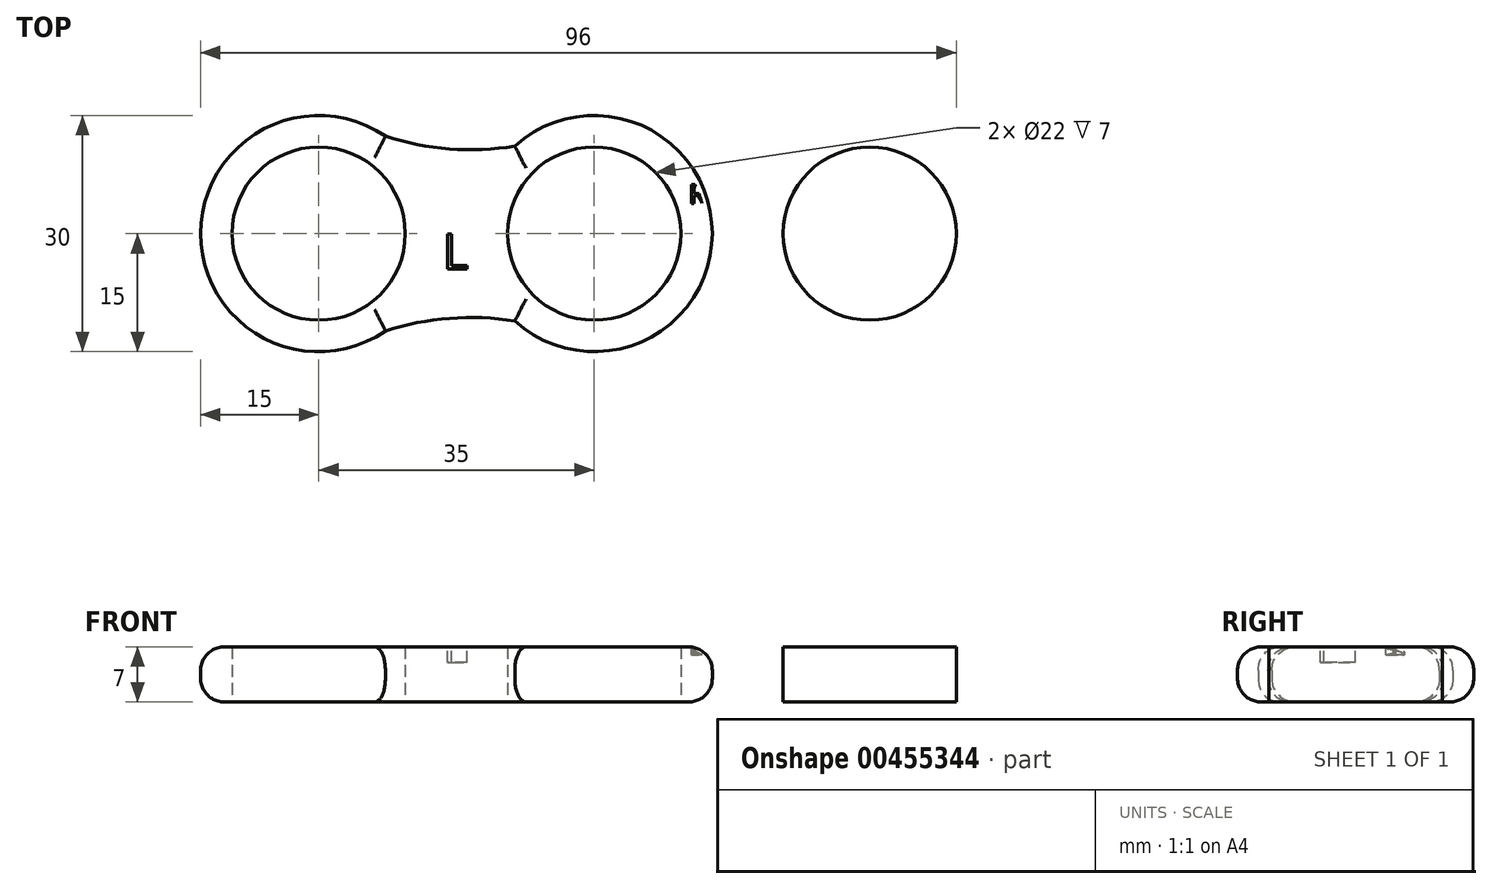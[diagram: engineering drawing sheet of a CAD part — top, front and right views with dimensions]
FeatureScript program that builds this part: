
annotation { "Feature Type Name" : "Feature", "Feature Type Description" : "" }
export const myFeature = defineFeature(function(context is Context, id is Id, definition is map)
    precondition{}
    {
        {
            var Q0;
            Q0=qCreatedBy(makeId("Top.planeOp"),FACE);
            var sketch = newSketch(context, id + "F0", { "sketchPlane" : qUnion([Q0])});
            skPoint(sketch, "E0.middle", {"position": v(0, 0) * mm});
            skCircle(sketch, "E1", {"center": v(0, 0) * mm, "radius": 11 * mm});
            skCircle(sketch, "E2", {"center": v(0, 0) * mm, "radius": 15 * mm});
            skCircle(sketch, "E3", {"center": v(-35, 0) * mm, "radius": 11 * mm});
            skCircle(sketch, "E4", {"center": v(-35, 0) * mm, "radius": 15 * mm});
            skArc(sketch, "E5", {"start": v(-26.52, 12.37) * mm, "mid": v(-18.37, 10.76) * mm, "end": v(-10.08, 11.11) * mm});
            skArc(sketch, "E6.MirrorCS", {"start": v(-26.52, -12.37) * mm, "mid": v(-18.37, -10.76) * mm, "end": v(-10.08, -11.11) * mm});
            skArc(sketch, "E7.MirrorCS", {"start": v(26.52, 12.37) * mm, "mid": v(18.37, 10.76) * mm, "end": v(10.08, 11.11) * mm});
            skArc(sketch, "E8.MirrorCS", {"start": v(26.52, -12.37) * mm, "mid": v(18.37, -10.76) * mm, "end": v(10.08, -11.11) * mm});
            skCircle(sketch, "E9.MirrorC", {"center": v(35, 0) * mm, "radius": 15 * mm});
            skCircle(sketch, "E10.MirrorC", {"center": v(35, 0) * mm, "radius": 11 * mm});
            skSolve(sketch);
        }
        {
            var Q0;
            Q0=makeQuery(id+"F0.imprint","IMPRINT",FACE,{"disambiguationData":[TD([[makeQuery(id+"F0.imprint","IMPRINT",EDGE,{"derivedFrom":sQuery(id+"F0.wireOp",EDGE,"cd22e090-de5e-44ce-a2e8-da55deea97581.MirrorC")}),1.0]])]});
            var Q1;
            Q1=makeQuery(id+"F0.imprint","IMPRINT",FACE,{"disambiguationData":[TD([[makeQuery(id+"F0.imprint","IMPRINT",EDGE,{"derivedFrom":sQuery(id+"F0.wireOp",EDGE,"E1")}),-1.0]])]});
            var Q2;
            {var subQ0=sQuery(id+"F0.wireOp",EDGE,"e8e17bcd-66d5-45fb-b403-fcb8348c6d070.MirrorCS");Q2=makeQuery(id+"F0.imprint","IMPRINT",FACE,{"disambiguationData":[TD([[makeQuery(id+"F0.imprint","IMPRINT",EDGE,{"derivedFrom":subQ0}),-1.0]])]});}
            var Q3;
            {var subQ0=sQuery(id+"F0.wireOp",EDGE,"E5");Q3=makeQuery(id+"F0.imprint","IMPRINT",FACE,{"disambiguationData":[TD([[makeQuery(id+"F0.imprint","IMPRINT",EDGE,{"derivedFrom":subQ0}),-1.0]])]});}
            var Q4;
            Q4=makeQuery(id+"F0.imprint","IMPRINT",FACE,{"disambiguationData":[TD([[makeQuery(id+"F0.imprint","IMPRINT",EDGE,{"derivedFrom":sQuery(id+"F0.wireOp",EDGE,"E3")}),-1.0]])]});
            var Q5;
            Q5=makeQuery(id+"F0.imprint","IMPRINT",FACE,{"disambiguationData":[TD([[makeQuery(id+"F0.imprint","IMPRINT",EDGE,{"derivedFrom":sQuery(id+"F0.wireOp",EDGE,"E10.MirrorC")}),1.0]])]});
            var Q6;
            {var subQ0=sQuery(id+"F0.wireOp",EDGE,"E7.MirrorCS");Q6=makeQuery(id+"F0.imprint","IMPRINT",FACE,{"disambiguationData":[TD([[makeQuery(id+"F0.imprint","IMPRINT",EDGE,{"derivedFrom":subQ0}),1.0]])]});}
            extrude(context, id + "F1", {"entities" : qUnion([Q0, Q1, Q2, Q3, Q4, Q5, Q6]), "depth" : 7 * mm});
        }
        {
            var Q0;
            Q0=makeQuery(id+"F1.opExtrude","CAP_EDGE",EDGE,{"disambiguationData":[OSD([sQuery(id+"F0.wireOp",EDGE,"E5")])],"isStart":true});
            var Q1;
            Q1=makeQuery(id+"F1.opExtrude","CAP_EDGE",EDGE,{"disambiguationData":[OSD([sQuery(id+"F0.wireOp",EDGE,"E4")])],"isStart":true});
            var Q2;
            Q2=makeQuery(id+"F1.opExtrude","CAP_EDGE",EDGE,{"disambiguationData":[OSD([sQuery(id+"F0.wireOp",EDGE,"E6.MirrorCS")])],"isStart":true});
            var Q3;
            {var subQ0=sQuery(id+"F0.wireOp",EDGE,"E2");Q3=makeQuery(id+"F1.opExtrude","CAP_EDGE",EDGE,{"disambiguationData":[OSD([subQ0]),TDD([makeQuery(id+"F0.imprint","IMPRINT",EDGE,{"disambiguationData":[TD([[makeQuery(id+"F0.imprint","INTERSECT",VERTEX,{"derivedFrom":[subQ0,sQuery(id+"F0.wireOp",EDGE,"E6.MirrorCS")]}),-1.0]])],"derivedFrom":subQ0})])],"isStart":true});}
            var Q4;
            Q4=makeQuery(id+"F1.opExtrude","CAP_EDGE",EDGE,{"disambiguationData":[OSD([sQuery(id+"F0.wireOp",EDGE,"E8.MirrorCS")])],"isStart":true});
            var Q5;
            Q5=makeQuery(id+"F1.opExtrude","CAP_EDGE",EDGE,{"disambiguationData":[OSD([sQuery(id+"F0.wireOp",EDGE,"E9.MirrorC")])],"isStart":true});
            var Q6;
            Q6=makeQuery(id+"F1.opExtrude","CAP_EDGE",EDGE,{"disambiguationData":[OSD([sQuery(id+"F0.wireOp",EDGE,"E7.MirrorCS")])],"isStart":true});
            var Q7;
            {var subQ0=sQuery(id+"F0.wireOp",EDGE,"E2");Q7=makeQuery(id+"F1.opExtrude","CAP_EDGE",EDGE,{"disambiguationData":[OSD([subQ0]),TDD([makeQuery(id+"F0.imprint","IMPRINT",EDGE,{"disambiguationData":[TD([[makeQuery(id+"F0.imprint","INTERSECT",VERTEX,{"derivedFrom":[subQ0,sQuery(id+"F0.wireOp",EDGE,"E5")]}),1.0]])],"derivedFrom":subQ0})])],"isStart":true});}
            fillet(context, id + "F2", {"entities" : qUnion([Q0, Q1, Q2, Q3, Q4, Q5, Q6, Q7]), "radius" : 3 * mm, "tangentPropagation" : true, "allowEdgeOverflow" : false});
        }
        {
            var Q0;
            Q0=makeQuery(id+"F1.opExtrude","CAP_EDGE",EDGE,{"disambiguationData":[OSD([sQuery(id+"F0.wireOp",EDGE,"E9.MirrorC")])],"isStart":false});
            var Q1;
            Q1=makeQuery(id+"F1.opExtrude","CAP_EDGE",EDGE,{"disambiguationData":[OSD([sQuery(id+"F0.wireOp",EDGE,"E8.MirrorCS")])],"isStart":false});
            var Q2;
            {var subQ0=sQuery(id+"F0.wireOp",EDGE,"E2");Q2=makeQuery(id+"F1.opExtrude","CAP_EDGE",EDGE,{"disambiguationData":[OSD([subQ0]),TDD([makeQuery(id+"F0.imprint","IMPRINT",EDGE,{"disambiguationData":[TD([[makeQuery(id+"F0.imprint","INTERSECT",VERTEX,{"derivedFrom":[subQ0,sQuery(id+"F0.wireOp",EDGE,"E6.MirrorCS")]}),-1.0]])],"derivedFrom":subQ0})])],"isStart":false});}
            var Q3;
            Q3=makeQuery(id+"F1.opExtrude","CAP_EDGE",EDGE,{"disambiguationData":[OSD([sQuery(id+"F0.wireOp",EDGE,"E6.MirrorCS")])],"isStart":false});
            var Q4;
            Q4=makeQuery(id+"F1.opExtrude","CAP_EDGE",EDGE,{"disambiguationData":[OSD([sQuery(id+"F0.wireOp",EDGE,"E4")])],"isStart":false});
            var Q5;
            Q5=makeQuery(id+"F1.opExtrude","CAP_EDGE",EDGE,{"disambiguationData":[OSD([sQuery(id+"F0.wireOp",EDGE,"E5")])],"isStart":false});
            var Q6;
            {var subQ0=sQuery(id+"F0.wireOp",EDGE,"E2");Q6=makeQuery(id+"F1.opExtrude","CAP_EDGE",EDGE,{"disambiguationData":[OSD([subQ0]),TDD([makeQuery(id+"F0.imprint","IMPRINT",EDGE,{"disambiguationData":[TD([[makeQuery(id+"F0.imprint","INTERSECT",VERTEX,{"derivedFrom":[subQ0,sQuery(id+"F0.wireOp",EDGE,"E5")]}),1.0]])],"derivedFrom":subQ0})])],"isStart":false});}
            var Q7;
            Q7=makeQuery(id+"F1.opExtrude","CAP_EDGE",EDGE,{"disambiguationData":[OSD([sQuery(id+"F0.wireOp",EDGE,"E7.MirrorCS")])],"isStart":false});
            fillet(context, id + "F3", {"entities" : qUnion([Q0, Q1, Q2, Q3, Q4, Q5, Q6, Q7]), "radius" : 3 * mm, "tangentPropagation" : true, "allowEdgeOverflow" : false});
        }
        {
            var Q0;
            Q0=makeQuery(id+"F1.opExtrude","CAP_FACE",FACE,{"disambiguationData":[OSD([sQuery(id+"F0.wireOp",EDGE,"E1"),sQuery(id+"F0.wireOp",EDGE,"E2"),sQuery(id+"F0.wireOp",EDGE,"E3"),sQuery(id+"F0.wireOp",EDGE,"E4"),sQuery(id+"F0.wireOp",EDGE,"E5"),sQuery(id+"F0.wireOp",EDGE,"E6.MirrorCS"),sQuery(id+"F0.wireOp",EDGE,"E7.MirrorCS"),sQuery(id+"F0.wireOp",EDGE,"E8.MirrorCS"),sQuery(id+"F0.wireOp",EDGE,"E9.MirrorC"),sQuery(id+"F0.wireOp",EDGE,"E10.MirrorC")])],"isStart":false});
            var sketch = newSketch(context, id + "F4", { "sketchPlane" : qUnion([Q0])});
            skText(sketch, "E11", { "text": "R.H.K", "fontName": "OpenSans-Regular.ttf"});
            const initialGuessF4  = {"E11": [0.01206, 0.00384, 1, 0, 0.00239]};
            skSetInitialGuess(sketch, initialGuessF4);
            skSolve(sketch);
        }
        {
            var Q0;
            Q0 = qSketchRegion(id + "F4", true);
            extrude(context, id + "F5", {"entities" : qUnion([Q0]), "operationType" : NewBodyOperationType.REMOVE, "oppositeDirection" : true, "depth" : 1 * mm});
        }
        {
            var Q0;
            {var subQ0=sQuery(id+"F0.wireOp",EDGE,"E8.MirrorCS");var subQ1=sQuery(id+"F0.wireOp",EDGE,"E7.MirrorCS");var subQ2=sQuery(id+"F0.wireOp",EDGE,"E5");var subQ3=sQuery(id+"F0.wireOp",EDGE,"E4");var subQ4=sQuery(id+"F0.wireOp",EDGE,"E6.MirrorCS");var subQ5=sQuery(id+"F0.wireOp",EDGE,"E2");var subQ6=sQuery(id+"F0.wireOp",EDGE,"E3");var subQ7=sQuery(id+"F0.wireOp",EDGE,"E1");var subQ8=sQuery(id+"F0.wireOp",EDGE,"E9.MirrorC");var subQ9=sQuery(id+"F0.wireOp",EDGE,"E10.MirrorC");Q0=makeQuery(id+"F5.boolean.opBoolean","SPLIT",FACE,{"disambiguationData":[TD([makeQuery(id+"F1.opExtrude","SWEPT_FACE",FACE,{"disambiguationData":[OSD([subQ7])]})])],"derivedFrom":makeQuery(id+"F1.opExtrude","CAP_FACE",FACE,{"disambiguationData":[OSD([subQ7,subQ5,subQ6,subQ3,subQ2,subQ4,subQ1,subQ0,subQ8,subQ9])],"isStart":false})});}
            var sketch = newSketch(context, id + "F6", { "sketchPlane" : qUnion([Q0])});
            skText(sketch, "E12", { "text": "L", "fontName": "OpenSans-Regular.ttf"});
            const initialGuessF6  = {"E12": [-0.01925, -0.0045, 1, 0, 0.0045]};
            skSetInitialGuess(sketch, initialGuessF6);
            skSolve(sketch);
        }
        {
            var Q0;
            Q0 = qSketchRegion(id + "F6", true);
            extrude(context, id + "F7", {"entities" : qUnion([Q0]), "operationType" : NewBodyOperationType.REMOVE, "oppositeDirection" : true, "depth" : 2 * mm});
        }
    });
